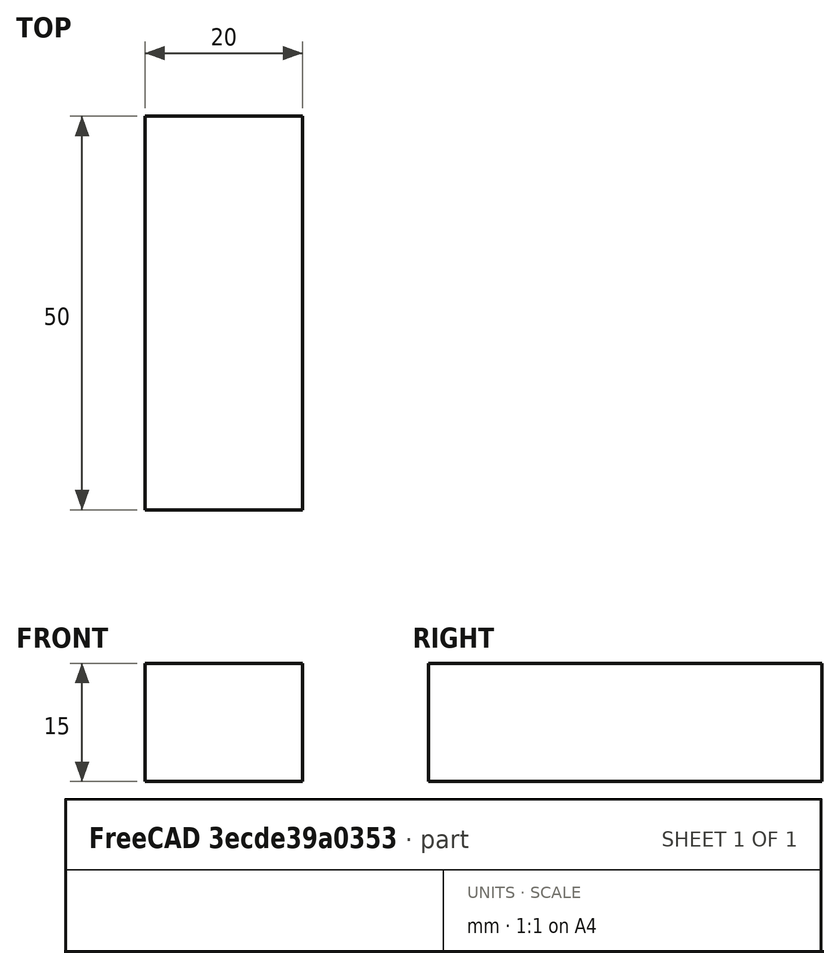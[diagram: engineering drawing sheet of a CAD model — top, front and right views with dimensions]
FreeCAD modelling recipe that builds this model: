
FCSTD DOCUMENT  (FreeCAD 1.0R39285 (Git))
Label: trial for varset
License: All rights reserved
LicenseURL: https://en.wikipedia.org/wiki/All_rights_reserved
objects: App::VarSet×1, Sketcher::SketchObject×1, PartDesign::Pad×1, PartDesign::Body×1
note: 6 computed .brp shape members not serialized (recipe doc carries the construction recipe); baked Part::Feature solids carry a one-line shape summary decoded from their .brp

FEATURE [App::VarSet] VarSet
  height = 15
  length = 50
  width = 20
FEATURE [Sketcher::SketchObject] Sketch
  ArcFitTolerance = 1e-06
  AttachmentSupport = -> [XY_Plane]
  FullyConstrained = true
  MakeInternals = false
  MapMode = 5
  expr: Constraints[10] = <<VarSet>>.length
  expr: Constraints[9] = <<VarSet>>.width
  sketch-geometry (4):
    g0: LineSegment StartX=0 StartY=0 StartZ=0 EndX=20 EndY=0 EndZ=0
    g1: LineSegment StartX=20 StartY=0 StartZ=0 EndX=20 EndY=50 EndZ=0
    g2: LineSegment StartX=20 StartY=50 StartZ=0 EndX=0 EndY=50 EndZ=0
    g3: LineSegment StartX=0 StartY=50 StartZ=0 EndX=0 EndY=0 EndZ=0
  constraints (11):
    c: Coincident(g0,g1)
    c: Coincident(g1,g2)
    c: Coincident(g2,g3)
    c: Coincident(g3,g0)
    c: Horizontal(g0)
    c: Horizontal(g2)
    c: Vertical(g1)
    c: Vertical(g3)
    c: Coincident(g0,g-1)
    c: DistanceX(g2,g2) = 20
    c: DistanceY(g1,g1) = 50
FEATURE [PartDesign::Pad] Pad
  Direction = (0,0,1)
  Length = 15
  Length2 = 10
  Profile = -> Sketch
  ReferenceAxis = -> Sketch [N_Axis]
  Refine = true
  Suppressed = false
  Type = 0
  expr: Length = <<VarSet>>.height
FEATURE [PartDesign::Body] Body
  AllowCompound = false
  Group = -> [VarSet,Sketch,Pad]
  Origin = -> Origin
  Tip = -> Pad
